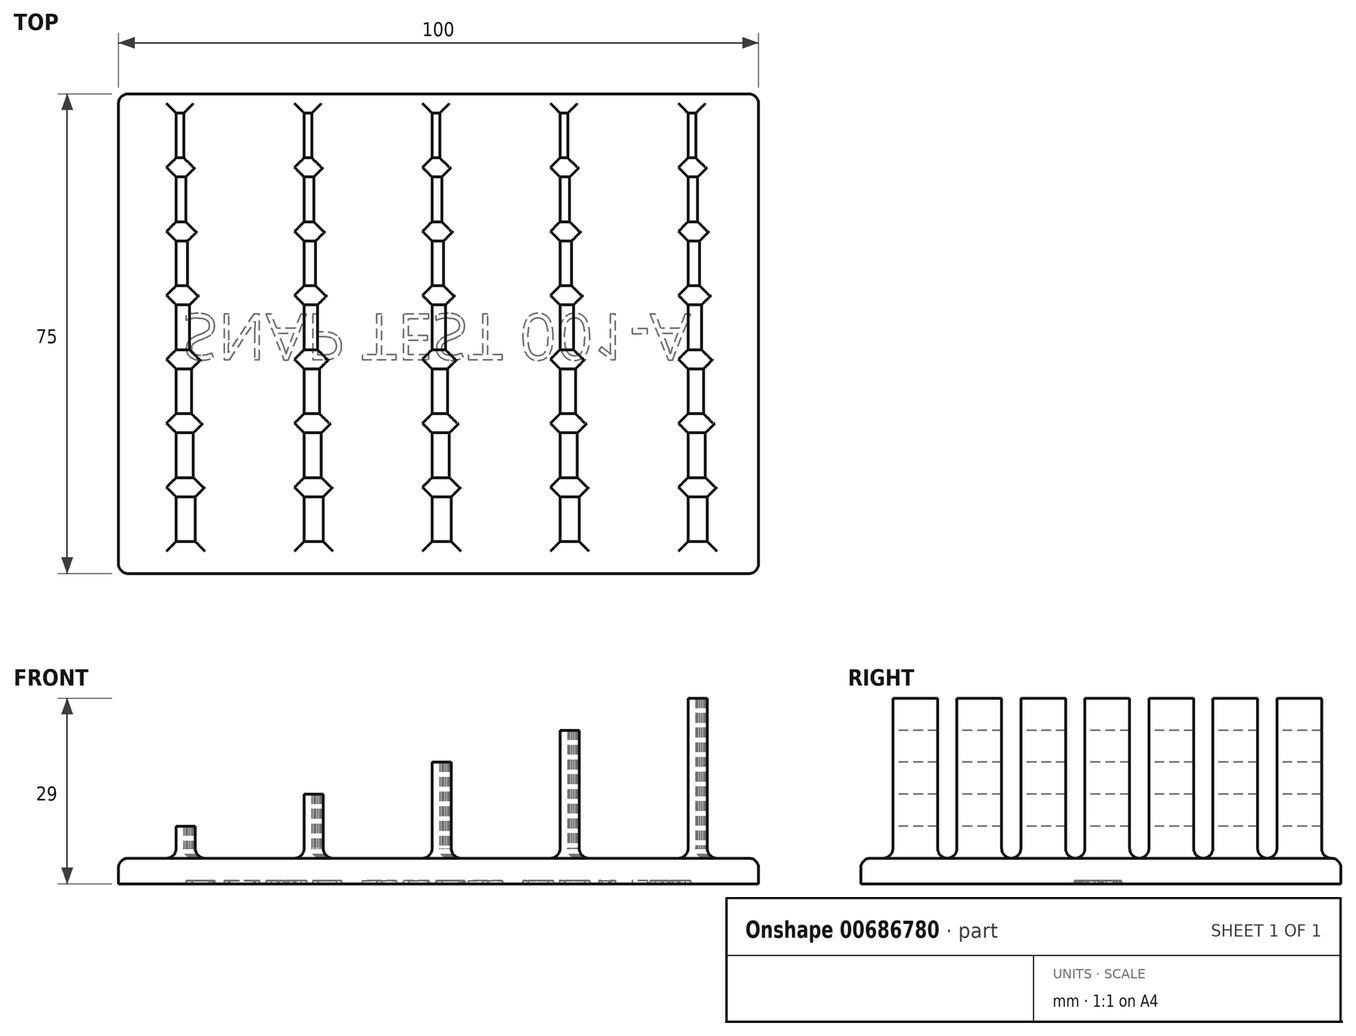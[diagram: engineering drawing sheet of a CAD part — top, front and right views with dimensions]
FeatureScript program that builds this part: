
annotation { "Feature Type Name" : "Feature", "Feature Type Description" : "" }
export const myFeature = defineFeature(function(context is Context, id is Id, definition is map)
    precondition{}
    {
        {
            var Q0;
            Q0=qCreatedBy(makeId("Top.planeOp"),FACE);
            var sketch = newSketch(context, id + "F0", { "sketchPlane" : qUnion([Q0])});
            skLineSegment(sketch, "E0.bottom", {"start": v(-50, 37.5) * mm, "end": v(50, 37.5) * mm});
            skLineSegment(sketch, "E0.top", {"start": v(-50, -37.5) * mm, "end": v(50, -37.5) * mm});
            skLineSegment(sketch, "E0.left", {"start": v(-50, 37.5) * mm, "end": v(-50, -37.5) * mm});
            skLineSegment(sketch, "E0.right", {"start": v(50, 37.5) * mm, "end": v(50, -37.5) * mm});
            skPoint(sketch, "E0.middle", {"position": v(0, 0) * mm});
            skSolve(sketch);
        }
        {
            var Q0;
            Q0=makeQuery(id+"F0.imprint","IMPRINT",FACE,{"disambiguationData":[TD([[makeQuery(id+"F0.imprint","IMPRINT",EDGE,{"derivedFrom":sQuery(id+"F0.wireOp",EDGE,"E0.bottom")}),-1.0]])]});
            extrude(context, id + "F1", {"entities" : qUnion([Q0]), "depth" : 4 * mm, "offsetDistance" : 25 * mm});
        }
        {
            var Q0;
            Q0=makeQuery(id+"F1.opExtrude","CAP_FACE",FACE,{"disambiguationData":[OSD([sQuery(id+"F0.wireOp",EDGE,"E0.bottom"),sQuery(id+"F0.wireOp",EDGE,"E0.top"),sQuery(id+"F0.wireOp",EDGE,"E0.left"),sQuery(id+"F0.wireOp",EDGE,"E0.right")])],"isStart":false});
            var sketch = newSketch(context, id + "F2", { "sketchPlane" : qUnion([Q0])});
            skLineSegment(sketch, "E1", {"start": v(-41, 37.5) * mm, "end": v(-41, -37.5) * mm, "construction": true});
            skLineSegment(sketch, "E2.bottom", {"start": v(-41, 34.5) * mm, "end": v(-39.8, 34.5) * mm});
            skLineSegment(sketch, "E2.top", {"start": v(-41, 27.5) * mm, "end": v(-39.8, 27.5) * mm});
            skLineSegment(sketch, "E2.left", {"start": v(-41, 34.5) * mm, "end": v(-41, 27.5) * mm});
            skLineSegment(sketch, "E2.right", {"start": v(-39.8, 34.5) * mm, "end": v(-39.8, 27.5) * mm});
            skLineSegment(sketch, "E3.bottom", {"start": v(-41, 24.5) * mm, "end": v(-39.5, 24.5) * mm});
            skLineSegment(sketch, "E3.top", {"start": v(-41, 17.5) * mm, "end": v(-39.5, 17.5) * mm});
            skLineSegment(sketch, "E3.left", {"start": v(-41, 24.5) * mm, "end": v(-41, 17.5) * mm});
            skLineSegment(sketch, "E3.right", {"start": v(-39.5, 24.5) * mm, "end": v(-39.5, 17.5) * mm});
            skLineSegment(sketch, "E4.bottom", {"start": v(-41, 14.5) * mm, "end": v(-39.2, 14.5) * mm});
            skLineSegment(sketch, "E4.top", {"start": v(-41, 7.5) * mm, "end": v(-39.2, 7.5) * mm});
            skLineSegment(sketch, "E4.left", {"start": v(-41, 14.5) * mm, "end": v(-41, 7.5) * mm});
            skLineSegment(sketch, "E4.right", {"start": v(-39.2, 14.5) * mm, "end": v(-39.2, 7.5) * mm});
            skLineSegment(sketch, "E5.bottom", {"start": v(-41, 4.5) * mm, "end": v(-38.9, 4.5) * mm});
            skLineSegment(sketch, "E5.top", {"start": v(-41, -2.5) * mm, "end": v(-38.9, -2.5) * mm});
            skLineSegment(sketch, "E5.left", {"start": v(-41, 4.5) * mm, "end": v(-41, -2.5) * mm});
            skLineSegment(sketch, "E5.right", {"start": v(-38.9, 4.5) * mm, "end": v(-38.9, -2.5) * mm});
            skLineSegment(sketch, "E6.bottom", {"start": v(-41, -5.5) * mm, "end": v(-38.6, -5.5) * mm});
            skLineSegment(sketch, "E6.top", {"start": v(-41, -12.5) * mm, "end": v(-38.6, -12.5) * mm});
            skLineSegment(sketch, "E6.left", {"start": v(-41, -5.5) * mm, "end": v(-41, -12.5) * mm});
            skLineSegment(sketch, "E6.right", {"start": v(-38.6, -5.5) * mm, "end": v(-38.6, -12.5) * mm});
            skLineSegment(sketch, "E7.bottom", {"start": v(-41, -15.5) * mm, "end": v(-38.3, -15.5) * mm});
            skLineSegment(sketch, "E7.top", {"start": v(-41, -22.5) * mm, "end": v(-38.3, -22.5) * mm});
            skLineSegment(sketch, "E7.left", {"start": v(-41, -15.5) * mm, "end": v(-41, -22.5) * mm});
            skLineSegment(sketch, "E7.right", {"start": v(-38.3, -15.5) * mm, "end": v(-38.3, -22.5) * mm});
            skLineSegment(sketch, "E8.bottom", {"start": v(-41, -25.5) * mm, "end": v(-38, -25.5) * mm});
            skLineSegment(sketch, "E8.top", {"start": v(-41, -32.5) * mm, "end": v(-38, -32.5) * mm});
            skLineSegment(sketch, "E8.left", {"start": v(-41, -25.5) * mm, "end": v(-41, -32.5) * mm});
            skLineSegment(sketch, "E8.right", {"start": v(-38, -25.5) * mm, "end": v(-38, -32.5) * mm});
            skLineSegment(sketch, "E9.1.0.0", {"start": v(-18.9, 4.5) * mm, "end": v(-18.9, -2.5) * mm});
            skLineSegment(sketch, "E9.1.0.1", {"start": v(-21, 14.5) * mm, "end": v(-21, 7.5) * mm});
            skLineSegment(sketch, "E9.1.0.2", {"start": v(-21, -25.5) * mm, "end": v(-18, -25.5) * mm});
            skLineSegment(sketch, "E9.1.0.3", {"start": v(-19.2, 14.5) * mm, "end": v(-19.2, 7.5) * mm});
            skLineSegment(sketch, "E9.1.0.4", {"start": v(-18, -25.5) * mm, "end": v(-18, -32.5) * mm});
            skLineSegment(sketch, "E9.1.0.5", {"start": v(-21, -15.5) * mm, "end": v(-18.3, -15.5) * mm});
            skLineSegment(sketch, "E9.1.0.6", {"start": v(-21, -5.5) * mm, "end": v(-18.6, -5.5) * mm});
            skLineSegment(sketch, "E9.1.0.7", {"start": v(-21, -32.5) * mm, "end": v(-18, -32.5) * mm});
            skLineSegment(sketch, "E9.1.0.8", {"start": v(-21, -5.5) * mm, "end": v(-21, -12.5) * mm});
            skLineSegment(sketch, "E9.1.0.9", {"start": v(-21, -12.5) * mm, "end": v(-18.6, -12.5) * mm});
            skLineSegment(sketch, "E9.1.0.10", {"start": v(-18.3, -15.5) * mm, "end": v(-18.3, -22.5) * mm});
            skLineSegment(sketch, "E9.1.0.11", {"start": v(-21, -22.5) * mm, "end": v(-18.3, -22.5) * mm});
            skLineSegment(sketch, "E9.1.0.12", {"start": v(-21, 4.5) * mm, "end": v(-21, -2.5) * mm});
            skLineSegment(sketch, "E9.1.0.13", {"start": v(-18.6, -5.5) * mm, "end": v(-18.6, -12.5) * mm});
            skLineSegment(sketch, "E9.1.0.14", {"start": v(-21, -15.5) * mm, "end": v(-21, -22.5) * mm});
            skLineSegment(sketch, "E9.1.0.15", {"start": v(-21, -25.5) * mm, "end": v(-21, -32.5) * mm});
            skLineSegment(sketch, "E9.1.0.16", {"start": v(-19.5, 24.5) * mm, "end": v(-19.5, 17.5) * mm});
            skLineSegment(sketch, "E9.1.0.17", {"start": v(-21, 24.5) * mm, "end": v(-21, 17.5) * mm});
            skLineSegment(sketch, "E9.1.0.18", {"start": v(-21, 34.5) * mm, "end": v(-21, 27.5) * mm});
            skLineSegment(sketch, "E9.1.0.19", {"start": v(-19.8, 34.5) * mm, "end": v(-19.8, 27.5) * mm});
            skLineSegment(sketch, "E9.1.0.20", {"start": v(-21, 7.5) * mm, "end": v(-19.2, 7.5) * mm});
            skLineSegment(sketch, "E9.1.0.21", {"start": v(-21, -2.5) * mm, "end": v(-18.9, -2.5) * mm});
            skLineSegment(sketch, "E9.1.0.22", {"start": v(-21, 4.5) * mm, "end": v(-18.9, 4.5) * mm});
            skLineSegment(sketch, "E9.1.0.23", {"start": v(-21, 34.5) * mm, "end": v(-19.8, 34.5) * mm});
            skLineSegment(sketch, "E9.1.0.24", {"start": v(-21, 27.5) * mm, "end": v(-19.8, 27.5) * mm});
            skLineSegment(sketch, "E9.1.0.25", {"start": v(-21, 14.5) * mm, "end": v(-19.2, 14.5) * mm});
            skLineSegment(sketch, "E9.1.0.26", {"start": v(-21, 24.5) * mm, "end": v(-19.5, 24.5) * mm});
            skLineSegment(sketch, "E9.1.0.27", {"start": v(-21, 17.5) * mm, "end": v(-19.5, 17.5) * mm});
            skLineSegment(sketch, "E9.2.0.0", {"start": v(1.1, 4.5) * mm, "end": v(1.1, -2.5) * mm});
            skLineSegment(sketch, "E9.2.0.1", {"start": v(-1, 14.5) * mm, "end": v(-1, 7.5) * mm});
            skLineSegment(sketch, "E9.2.0.2", {"start": v(-1, -25.5) * mm, "end": v(2, -25.5) * mm});
            skLineSegment(sketch, "E9.2.0.3", {"start": v(0.8, 14.5) * mm, "end": v(0.8, 7.5) * mm});
            skLineSegment(sketch, "E9.2.0.4", {"start": v(2, -25.5) * mm, "end": v(2, -32.5) * mm});
            skLineSegment(sketch, "E9.2.0.5", {"start": v(-1, -15.5) * mm, "end": v(1.7, -15.5) * mm});
            skLineSegment(sketch, "E9.2.0.6", {"start": v(-1, -5.5) * mm, "end": v(1.4, -5.5) * mm});
            skLineSegment(sketch, "E9.2.0.7", {"start": v(-1, -32.5) * mm, "end": v(2, -32.5) * mm});
            skLineSegment(sketch, "E9.2.0.8", {"start": v(-1, -5.5) * mm, "end": v(-1, -12.5) * mm});
            skLineSegment(sketch, "E9.2.0.9", {"start": v(-1, -12.5) * mm, "end": v(1.4, -12.5) * mm});
            skLineSegment(sketch, "E9.2.0.10", {"start": v(1.7, -15.5) * mm, "end": v(1.7, -22.5) * mm});
            skLineSegment(sketch, "E9.2.0.11", {"start": v(-1, -22.5) * mm, "end": v(1.7, -22.5) * mm});
            skLineSegment(sketch, "E9.2.0.12", {"start": v(-1, 4.5) * mm, "end": v(-1, -2.5) * mm});
            skLineSegment(sketch, "E9.2.0.13", {"start": v(1.4, -5.5) * mm, "end": v(1.4, -12.5) * mm});
            skLineSegment(sketch, "E9.2.0.14", {"start": v(-1, -15.5) * mm, "end": v(-1, -22.5) * mm});
            skLineSegment(sketch, "E9.2.0.15", {"start": v(-1, -25.5) * mm, "end": v(-1, -32.5) * mm});
            skLineSegment(sketch, "E9.2.0.16", {"start": v(0.5, 24.5) * mm, "end": v(0.5, 17.5) * mm});
            skLineSegment(sketch, "E9.2.0.17", {"start": v(-1, 24.5) * mm, "end": v(-1, 17.5) * mm});
            skLineSegment(sketch, "E9.2.0.18", {"start": v(-1, 34.5) * mm, "end": v(-1, 27.5) * mm});
            skLineSegment(sketch, "E9.2.0.19", {"start": v(0.2, 34.5) * mm, "end": v(0.2, 27.5) * mm});
            skLineSegment(sketch, "E9.2.0.20", {"start": v(-1, 7.5) * mm, "end": v(0.8, 7.5) * mm});
            skLineSegment(sketch, "E9.2.0.21", {"start": v(-1, -2.5) * mm, "end": v(1.1, -2.5) * mm});
            skLineSegment(sketch, "E9.2.0.22", {"start": v(-1, 4.5) * mm, "end": v(1.1, 4.5) * mm});
            skLineSegment(sketch, "E9.2.0.23", {"start": v(-1, 34.5) * mm, "end": v(0.2, 34.5) * mm});
            skLineSegment(sketch, "E9.2.0.24", {"start": v(-1, 27.5) * mm, "end": v(0.2, 27.5) * mm});
            skLineSegment(sketch, "E9.2.0.25", {"start": v(-1, 14.5) * mm, "end": v(0.8, 14.5) * mm});
            skLineSegment(sketch, "E9.2.0.26", {"start": v(-1, 24.5) * mm, "end": v(0.5, 24.5) * mm});
            skLineSegment(sketch, "E9.2.0.27", {"start": v(-1, 17.5) * mm, "end": v(0.5, 17.5) * mm});
            skLineSegment(sketch, "E9.3.0.0", {"start": v(21.1, 4.5) * mm, "end": v(21.1, -2.5) * mm});
            skLineSegment(sketch, "E9.3.0.1", {"start": v(19, 14.5) * mm, "end": v(19, 7.5) * mm});
            skLineSegment(sketch, "E9.3.0.2", {"start": v(19, -25.5) * mm, "end": v(22, -25.5) * mm});
            skLineSegment(sketch, "E9.3.0.3", {"start": v(20.8, 14.5) * mm, "end": v(20.8, 7.5) * mm});
            skLineSegment(sketch, "E9.3.0.4", {"start": v(22, -25.5) * mm, "end": v(22, -32.5) * mm});
            skLineSegment(sketch, "E9.3.0.5", {"start": v(19, -15.5) * mm, "end": v(21.7, -15.5) * mm});
            skLineSegment(sketch, "E9.3.0.6", {"start": v(19, -5.5) * mm, "end": v(21.4, -5.5) * mm});
            skLineSegment(sketch, "E9.3.0.7", {"start": v(19, -32.5) * mm, "end": v(22, -32.5) * mm});
            skLineSegment(sketch, "E9.3.0.8", {"start": v(19, -5.5) * mm, "end": v(19, -12.5) * mm});
            skLineSegment(sketch, "E9.3.0.9", {"start": v(19, -12.5) * mm, "end": v(21.4, -12.5) * mm});
            skLineSegment(sketch, "E9.3.0.10", {"start": v(21.7, -15.5) * mm, "end": v(21.7, -22.5) * mm});
            skLineSegment(sketch, "E9.3.0.11", {"start": v(19, -22.5) * mm, "end": v(21.7, -22.5) * mm});
            skLineSegment(sketch, "E9.3.0.12", {"start": v(19, 4.5) * mm, "end": v(19, -2.5) * mm});
            skLineSegment(sketch, "E9.3.0.13", {"start": v(21.4, -5.5) * mm, "end": v(21.4, -12.5) * mm});
            skLineSegment(sketch, "E9.3.0.14", {"start": v(19, -15.5) * mm, "end": v(19, -22.5) * mm});
            skLineSegment(sketch, "E9.3.0.15", {"start": v(19, -25.5) * mm, "end": v(19, -32.5) * mm});
            skLineSegment(sketch, "E9.3.0.16", {"start": v(20.5, 24.5) * mm, "end": v(20.5, 17.5) * mm});
            skLineSegment(sketch, "E9.3.0.17", {"start": v(19, 24.5) * mm, "end": v(19, 17.5) * mm});
            skLineSegment(sketch, "E9.3.0.18", {"start": v(19, 34.5) * mm, "end": v(19, 27.5) * mm});
            skLineSegment(sketch, "E9.3.0.19", {"start": v(20.2, 34.5) * mm, "end": v(20.2, 27.5) * mm});
            skLineSegment(sketch, "E9.3.0.20", {"start": v(19, 7.5) * mm, "end": v(20.8, 7.5) * mm});
            skLineSegment(sketch, "E9.3.0.21", {"start": v(19, -2.5) * mm, "end": v(21.1, -2.5) * mm});
            skLineSegment(sketch, "E9.3.0.22", {"start": v(19, 4.5) * mm, "end": v(21.1, 4.5) * mm});
            skLineSegment(sketch, "E9.3.0.23", {"start": v(19, 34.5) * mm, "end": v(20.2, 34.5) * mm});
            skLineSegment(sketch, "E9.3.0.24", {"start": v(19, 27.5) * mm, "end": v(20.2, 27.5) * mm});
            skLineSegment(sketch, "E9.3.0.25", {"start": v(19, 14.5) * mm, "end": v(20.8, 14.5) * mm});
            skLineSegment(sketch, "E9.3.0.26", {"start": v(19, 24.5) * mm, "end": v(20.5, 24.5) * mm});
            skLineSegment(sketch, "E9.3.0.27", {"start": v(19, 17.5) * mm, "end": v(20.5, 17.5) * mm});
            skLineSegment(sketch, "E9.4.0.0", {"start": v(41.1, 4.5) * mm, "end": v(41.1, -2.5) * mm});
            skLineSegment(sketch, "E9.4.0.1", {"start": v(39, 14.5) * mm, "end": v(39, 7.5) * mm});
            skLineSegment(sketch, "E9.4.0.2", {"start": v(39, -25.5) * mm, "end": v(42, -25.5) * mm});
            skLineSegment(sketch, "E9.4.0.3", {"start": v(40.8, 14.5) * mm, "end": v(40.8, 7.5) * mm});
            skLineSegment(sketch, "E9.4.0.4", {"start": v(42, -25.5) * mm, "end": v(42, -32.5) * mm});
            skLineSegment(sketch, "E9.4.0.5", {"start": v(39, -15.5) * mm, "end": v(41.7, -15.5) * mm});
            skLineSegment(sketch, "E9.4.0.6", {"start": v(39, -5.5) * mm, "end": v(41.4, -5.5) * mm});
            skLineSegment(sketch, "E9.4.0.7", {"start": v(39, -32.5) * mm, "end": v(42, -32.5) * mm});
            skLineSegment(sketch, "E9.4.0.8", {"start": v(39, -5.5) * mm, "end": v(39, -12.5) * mm});
            skLineSegment(sketch, "E9.4.0.9", {"start": v(39, -12.5) * mm, "end": v(41.4, -12.5) * mm});
            skLineSegment(sketch, "E9.4.0.10", {"start": v(41.7, -15.5) * mm, "end": v(41.7, -22.5) * mm});
            skLineSegment(sketch, "E9.4.0.11", {"start": v(39, -22.5) * mm, "end": v(41.7, -22.5) * mm});
            skLineSegment(sketch, "E9.4.0.12", {"start": v(39, 4.5) * mm, "end": v(39, -2.5) * mm});
            skLineSegment(sketch, "E9.4.0.13", {"start": v(41.4, -5.5) * mm, "end": v(41.4, -12.5) * mm});
            skLineSegment(sketch, "E9.4.0.14", {"start": v(39, -15.5) * mm, "end": v(39, -22.5) * mm});
            skLineSegment(sketch, "E9.4.0.15", {"start": v(39, -25.5) * mm, "end": v(39, -32.5) * mm});
            skLineSegment(sketch, "E9.4.0.16", {"start": v(40.5, 24.5) * mm, "end": v(40.5, 17.5) * mm});
            skLineSegment(sketch, "E9.4.0.17", {"start": v(39, 24.5) * mm, "end": v(39, 17.5) * mm});
            skLineSegment(sketch, "E9.4.0.18", {"start": v(39, 34.5) * mm, "end": v(39, 27.5) * mm});
            skLineSegment(sketch, "E9.4.0.19", {"start": v(40.2, 34.5) * mm, "end": v(40.2, 27.5) * mm});
            skLineSegment(sketch, "E9.4.0.20", {"start": v(39, 7.5) * mm, "end": v(40.8, 7.5) * mm});
            skLineSegment(sketch, "E9.4.0.21", {"start": v(39, -2.5) * mm, "end": v(41.1, -2.5) * mm});
            skLineSegment(sketch, "E9.4.0.22", {"start": v(39, 4.5) * mm, "end": v(41.1, 4.5) * mm});
            skLineSegment(sketch, "E9.4.0.23", {"start": v(39, 34.5) * mm, "end": v(40.2, 34.5) * mm});
            skLineSegment(sketch, "E9.4.0.24", {"start": v(39, 27.5) * mm, "end": v(40.2, 27.5) * mm});
            skLineSegment(sketch, "E9.4.0.25", {"start": v(39, 14.5) * mm, "end": v(40.8, 14.5) * mm});
            skLineSegment(sketch, "E9.4.0.26", {"start": v(39, 24.5) * mm, "end": v(40.5, 24.5) * mm});
            skLineSegment(sketch, "E9.4.0.27", {"start": v(39, 17.5) * mm, "end": v(40.5, 17.5) * mm});
            skLineSegment(sketch, "E9.direction1", {"start": v(-41, -32.5) * mm, "end": v(-21, -32.5) * mm, "construction": true});
            skSolve(sketch);
        }
        {
            var Q0;
            Q0=makeQuery(id+"F2.imprint","IMPRINT",FACE,{"disambiguationData":[TD([[makeQuery(id+"F2.imprint","IMPRINT",EDGE,{"derivedFrom":sQuery(id+"F2.wireOp",EDGE,"E6.bottom")}),-1.0]])]});
            var Q1;
            Q1=makeQuery(id+"F2.imprint","IMPRINT",FACE,{"disambiguationData":[TD([[makeQuery(id+"F2.imprint","IMPRINT",EDGE,{"derivedFrom":sQuery(id+"F2.wireOp",EDGE,"E8.bottom")}),-1.0]])]});
            var Q2;
            Q2=makeQuery(id+"F2.imprint","IMPRINT",FACE,{"disambiguationData":[TD([[makeQuery(id+"F2.imprint","IMPRINT",EDGE,{"derivedFrom":sQuery(id+"F2.wireOp",EDGE,"E4.bottom")}),-1.0]])]});
            var Q3;
            Q3=makeQuery(id+"F2.imprint","IMPRINT",FACE,{"disambiguationData":[TD([[makeQuery(id+"F2.imprint","IMPRINT",EDGE,{"derivedFrom":sQuery(id+"F2.wireOp",EDGE,"E2.bottom")}),-1.0]])]});
            var Q4;
            Q4=makeQuery(id+"F2.imprint","IMPRINT",FACE,{"disambiguationData":[TD([[makeQuery(id+"F2.imprint","IMPRINT",EDGE,{"derivedFrom":sQuery(id+"F2.wireOp",EDGE,"E3.bottom")}),-1.0]])]});
            var Q5;
            Q5=makeQuery(id+"F2.imprint","IMPRINT",FACE,{"disambiguationData":[TD([[makeQuery(id+"F2.imprint","IMPRINT",EDGE,{"derivedFrom":sQuery(id+"F2.wireOp",EDGE,"E7.bottom")}),-1.0]])]});
            var Q6;
            Q6=makeQuery(id+"F2.imprint","IMPRINT",FACE,{"disambiguationData":[TD([[makeQuery(id+"F2.imprint","IMPRINT",EDGE,{"derivedFrom":sQuery(id+"F2.wireOp",EDGE,"E5.bottom")}),-1.0]])]});
            extrude(context, id + "F3", {"entities" : qUnion([Q0, Q1, Q2, Q3, Q4, Q5, Q6]), "operationType" : NewBodyOperationType.ADD, "depth" : 5 * mm, "offsetDistance" : 25 * mm});
        }
        {
            var Q0;
            Q0=makeQuery(id+"F2.imprint","IMPRINT",FACE,{"disambiguationData":[TD([[makeQuery(id+"F2.imprint","IMPRINT",EDGE,{"derivedFrom":sQuery(id+"F2.wireOp",EDGE,"E9.1.0.16")}),-1.0]])]});
            var Q1;
            Q1=makeQuery(id+"F2.imprint","IMPRINT",FACE,{"disambiguationData":[TD([[makeQuery(id+"F2.imprint","IMPRINT",EDGE,{"derivedFrom":sQuery(id+"F2.wireOp",EDGE,"E9.1.0.5")}),-1.0]])]});
            var Q2;
            Q2=makeQuery(id+"F2.imprint","IMPRINT",FACE,{"disambiguationData":[TD([[makeQuery(id+"F2.imprint","IMPRINT",EDGE,{"derivedFrom":sQuery(id+"F2.wireOp",EDGE,"E9.1.0.0")}),-1.0]])]});
            var Q3;
            Q3=makeQuery(id+"F2.imprint","IMPRINT",FACE,{"disambiguationData":[TD([[makeQuery(id+"F2.imprint","IMPRINT",EDGE,{"derivedFrom":sQuery(id+"F2.wireOp",EDGE,"E9.1.0.1")}),1.0]])]});
            var Q4;
            Q4=makeQuery(id+"F2.imprint","IMPRINT",FACE,{"disambiguationData":[TD([[makeQuery(id+"F2.imprint","IMPRINT",EDGE,{"derivedFrom":sQuery(id+"F2.wireOp",EDGE,"E9.1.0.2")}),-1.0]])]});
            var Q5;
            Q5=makeQuery(id+"F2.imprint","IMPRINT",FACE,{"disambiguationData":[TD([[makeQuery(id+"F2.imprint","IMPRINT",EDGE,{"derivedFrom":sQuery(id+"F2.wireOp",EDGE,"E9.1.0.18")}),1.0]])]});
            var Q6;
            Q6=makeQuery(id+"F2.imprint","IMPRINT",FACE,{"disambiguationData":[TD([[makeQuery(id+"F2.imprint","IMPRINT",EDGE,{"derivedFrom":sQuery(id+"F2.wireOp",EDGE,"E9.1.0.6")}),-1.0]])]});
            extrude(context, id + "F4", {"entities" : qUnion([Q0, Q1, Q2, Q3, Q4, Q5, Q6]), "operationType" : NewBodyOperationType.ADD, "depth" : 10 * mm, "offsetDistance" : 25 * mm});
        }
        {
            var Q0;
            Q0=makeQuery(id+"F2.imprint","IMPRINT",FACE,{"disambiguationData":[TD([[makeQuery(id+"F2.imprint","IMPRINT",EDGE,{"derivedFrom":sQuery(id+"F2.wireOp",EDGE,"E9.2.0.18")}),1.0]])]});
            var Q1;
            Q1=makeQuery(id+"F2.imprint","IMPRINT",FACE,{"disambiguationData":[TD([[makeQuery(id+"F2.imprint","IMPRINT",EDGE,{"derivedFrom":sQuery(id+"F2.wireOp",EDGE,"E9.2.0.1")}),1.0]])]});
            var Q2;
            Q2=makeQuery(id+"F2.imprint","IMPRINT",FACE,{"disambiguationData":[TD([[makeQuery(id+"F2.imprint","IMPRINT",EDGE,{"derivedFrom":sQuery(id+"F2.wireOp",EDGE,"E9.2.0.6")}),-1.0]])]});
            var Q3;
            Q3=makeQuery(id+"F2.imprint","IMPRINT",FACE,{"disambiguationData":[TD([[makeQuery(id+"F2.imprint","IMPRINT",EDGE,{"derivedFrom":sQuery(id+"F2.wireOp",EDGE,"E9.2.0.0")}),-1.0]])]});
            var Q4;
            Q4=makeQuery(id+"F2.imprint","IMPRINT",FACE,{"disambiguationData":[TD([[makeQuery(id+"F2.imprint","IMPRINT",EDGE,{"derivedFrom":sQuery(id+"F2.wireOp",EDGE,"E9.2.0.16")}),-1.0]])]});
            var Q5;
            Q5=makeQuery(id+"F2.imprint","IMPRINT",FACE,{"disambiguationData":[TD([[makeQuery(id+"F2.imprint","IMPRINT",EDGE,{"derivedFrom":sQuery(id+"F2.wireOp",EDGE,"E9.2.0.5")}),-1.0]])]});
            var Q6;
            Q6=makeQuery(id+"F2.imprint","IMPRINT",FACE,{"disambiguationData":[TD([[makeQuery(id+"F2.imprint","IMPRINT",EDGE,{"derivedFrom":sQuery(id+"F2.wireOp",EDGE,"E9.2.0.2")}),-1.0]])]});
            extrude(context, id + "F5", {"entities" : qUnion([Q0, Q1, Q2, Q3, Q4, Q5, Q6]), "operationType" : NewBodyOperationType.ADD, "depth" : 15 * mm, "offsetDistance" : 25 * mm});
        }
        {
            var Q0;
            Q0=makeQuery(id+"F2.imprint","IMPRINT",FACE,{"disambiguationData":[TD([[makeQuery(id+"F2.imprint","IMPRINT",EDGE,{"derivedFrom":sQuery(id+"F2.wireOp",EDGE,"E9.3.0.18")}),1.0]])]});
            var Q1;
            Q1=makeQuery(id+"F2.imprint","IMPRINT",FACE,{"disambiguationData":[TD([[makeQuery(id+"F2.imprint","IMPRINT",EDGE,{"derivedFrom":sQuery(id+"F2.wireOp",EDGE,"E9.3.0.16")}),-1.0]])]});
            var Q2;
            Q2=makeQuery(id+"F2.imprint","IMPRINT",FACE,{"disambiguationData":[TD([[makeQuery(id+"F2.imprint","IMPRINT",EDGE,{"derivedFrom":sQuery(id+"F2.wireOp",EDGE,"E9.3.0.6")}),-1.0]])]});
            var Q3;
            Q3=makeQuery(id+"F2.imprint","IMPRINT",FACE,{"disambiguationData":[TD([[makeQuery(id+"F2.imprint","IMPRINT",EDGE,{"derivedFrom":sQuery(id+"F2.wireOp",EDGE,"E9.3.0.5")}),-1.0]])]});
            var Q4;
            Q4=makeQuery(id+"F2.imprint","IMPRINT",FACE,{"disambiguationData":[TD([[makeQuery(id+"F2.imprint","IMPRINT",EDGE,{"derivedFrom":sQuery(id+"F2.wireOp",EDGE,"E9.3.0.2")}),-1.0]])]});
            var Q5;
            Q5=makeQuery(id+"F2.imprint","IMPRINT",FACE,{"disambiguationData":[TD([[makeQuery(id+"F2.imprint","IMPRINT",EDGE,{"derivedFrom":sQuery(id+"F2.wireOp",EDGE,"E9.3.0.1")}),1.0]])]});
            var Q6;
            Q6=makeQuery(id+"F2.imprint","IMPRINT",FACE,{"disambiguationData":[TD([[makeQuery(id+"F2.imprint","IMPRINT",EDGE,{"derivedFrom":sQuery(id+"F2.wireOp",EDGE,"E9.3.0.0")}),-1.0]])]});
            extrude(context, id + "F6", {"entities" : qUnion([Q0, Q1, Q2, Q3, Q4, Q5, Q6]), "operationType" : NewBodyOperationType.ADD, "depth" : 20 * mm, "offsetDistance" : 25 * mm});
        }
        {
            var Q0;
            Q0=makeQuery(id+"F2.imprint","IMPRINT",FACE,{"disambiguationData":[TD([[makeQuery(id+"F2.imprint","IMPRINT",EDGE,{"derivedFrom":sQuery(id+"F2.wireOp",EDGE,"E9.4.0.18")}),1.0]])]});
            var Q1;
            Q1=makeQuery(id+"F2.imprint","IMPRINT",FACE,{"disambiguationData":[TD([[makeQuery(id+"F2.imprint","IMPRINT",EDGE,{"derivedFrom":sQuery(id+"F2.wireOp",EDGE,"E9.4.0.16")}),-1.0]])]});
            var Q2;
            Q2=makeQuery(id+"F2.imprint","IMPRINT",FACE,{"disambiguationData":[TD([[makeQuery(id+"F2.imprint","IMPRINT",EDGE,{"derivedFrom":sQuery(id+"F2.wireOp",EDGE,"E9.4.0.6")}),-1.0]])]});
            var Q3;
            Q3=makeQuery(id+"F2.imprint","IMPRINT",FACE,{"disambiguationData":[TD([[makeQuery(id+"F2.imprint","IMPRINT",EDGE,{"derivedFrom":sQuery(id+"F2.wireOp",EDGE,"E9.4.0.0")}),-1.0]])]});
            var Q4;
            Q4=makeQuery(id+"F2.imprint","IMPRINT",FACE,{"disambiguationData":[TD([[makeQuery(id+"F2.imprint","IMPRINT",EDGE,{"derivedFrom":sQuery(id+"F2.wireOp",EDGE,"E9.4.0.2")}),-1.0]])]});
            var Q5;
            Q5=makeQuery(id+"F2.imprint","IMPRINT",FACE,{"disambiguationData":[TD([[makeQuery(id+"F2.imprint","IMPRINT",EDGE,{"derivedFrom":sQuery(id+"F2.wireOp",EDGE,"E9.4.0.1")}),1.0]])]});
            var Q6;
            Q6=makeQuery(id+"F2.imprint","IMPRINT",FACE,{"disambiguationData":[TD([[makeQuery(id+"F2.imprint","IMPRINT",EDGE,{"derivedFrom":sQuery(id+"F2.wireOp",EDGE,"E9.4.0.5")}),-1.0]])]});
            extrude(context, id + "F7", {"entities" : qUnion([Q0, Q1, Q2, Q3, Q4, Q5, Q6]), "operationType" : NewBodyOperationType.ADD, "depth" : 25 * mm, "offsetDistance" : 25 * mm});
        }
        {
            var Q0;
            Q0=makeQuery(id+"F1.opExtrude","CAP_FACE",FACE,{"disambiguationData":[OSD([sQuery(id+"F0.wireOp",EDGE,"E0.bottom"),sQuery(id+"F0.wireOp",EDGE,"E0.top"),sQuery(id+"F0.wireOp",EDGE,"E0.left"),sQuery(id+"F0.wireOp",EDGE,"E0.right")])],"isStart":false});
            fillet(context, id + "F8", {"entities" : qUnion([Q0]), "radius" : 1.5 * mm, "tangentPropagation" : true, "allowEdgeOverflow" : false});
        }
        {
            var Q0;
            Q0=makeQuery(id+"Fw7KeQQw6uLgcHZ_1.opShell","OFFSET_EDGE",EDGE,{"disambiguationData":[OSD([sQuery(id+"F0.wireOp",EDGE,"E0.top"),sQuery(id+"F0.wireOp",EDGE,"E0.left")])]});
            var Q1;
            Q1=makeQuery(id+"Fw7KeQQw6uLgcHZ_1.opShell","OFFSET_EDGE",EDGE,{"disambiguationData":[OSD([sQuery(id+"F0.wireOp",EDGE,"E0.bottom"),sQuery(id+"F0.wireOp",EDGE,"E0.left")])]});
            var Q2;
            Q2=makeQuery(id+"Fw7KeQQw6uLgcHZ_1.opShell","OFFSET_EDGE",EDGE,{"disambiguationData":[OSD([sQuery(id+"F0.wireOp",EDGE,"E0.bottom"),sQuery(id+"F0.wireOp",EDGE,"E0.right")])]});
            var Q3;
            Q3=makeQuery(id+"Fw7KeQQw6uLgcHZ_1.opShell","OFFSET_EDGE",EDGE,{"disambiguationData":[OSD([sQuery(id+"F0.wireOp",EDGE,"E0.top"),sQuery(id+"F0.wireOp",EDGE,"E0.right")])]});
            var Q4;
            Q4=makeQuery(id+"Fw7KeQQw6uLgcHZ_1.opShell","OFFSET_FACE",FACE,{"disambiguationData":[OSD([sQuery(id+"F0.wireOp",EDGE,"E0.bottom"),sQuery(id+"F0.wireOp",EDGE,"E0.top"),sQuery(id+"F0.wireOp",EDGE,"E0.left"),sQuery(id+"F0.wireOp",EDGE,"E0.right")])]});
            var Q5;
            Q5=makeQuery(id+"F1.opExtrude","SWEPT_EDGE",EDGE,{"disambiguationData":[OSD([sQuery(id+"F0.wireOp",EDGE,"E0.bottom"),sQuery(id+"F0.wireOp",EDGE,"E0.left")])]});
            var Q6;
            Q6=makeQuery(id+"F1.opExtrude","SWEPT_EDGE",EDGE,{"disambiguationData":[OSD([sQuery(id+"F0.wireOp",EDGE,"E0.bottom"),sQuery(id+"F0.wireOp",EDGE,"E0.right")])]});
            var Q7;
            Q7=makeQuery(id+"F1.opExtrude","SWEPT_EDGE",EDGE,{"disambiguationData":[OSD([sQuery(id+"F0.wireOp",EDGE,"E0.top"),sQuery(id+"F0.wireOp",EDGE,"E0.right")])]});
            var Q8;
            Q8=makeQuery(id+"F1.opExtrude","SWEPT_EDGE",EDGE,{"disambiguationData":[OSD([sQuery(id+"F0.wireOp",EDGE,"E0.top"),sQuery(id+"F0.wireOp",EDGE,"E0.left")])]});
            fillet(context, id + "F9", {"entities" : qUnion([Q0, Q1, Q2, Q3, Q4, Q5, Q6, Q7, Q8]), "radius" : 1.5 * mm, "tangentPropagation" : true, "allowEdgeOverflow" : false});
        }
        {
            var Q0;
            Q0=makeQuery(id+"F1.opExtrude","CAP_FACE",FACE,{"disambiguationData":[OSD([sQuery(id+"F0.wireOp",EDGE,"E0.bottom"),sQuery(id+"F0.wireOp",EDGE,"E0.top"),sQuery(id+"F0.wireOp",EDGE,"E0.left"),sQuery(id+"F0.wireOp",EDGE,"E0.right")])],"isStart":true});
            var sketch = newSketch(context, id + "F10", { "sketchPlane" : qUnion([Q0])});
            skText(sketch, "E10", { "text": "SNAP TEST 001-A", "fontName": "OpenSans-Regular.ttf"});
            const initialGuessF10  = {"E10": [-0.04, -0.00309, 1, 0, 0.0072]};
            skSetInitialGuess(sketch, initialGuessF10);
            skSolve(sketch);
        }
        {
            var Q0;
            Q0 = qSketchRegion(id + "F10", true);
            extrude(context, id + "F11", {"entities" : qUnion([Q0]), "operationType" : NewBodyOperationType.REMOVE, "oppositeDirection" : true, "depth" : .5 * mm, "offsetDistance" : 25 * mm});
        }
    });
